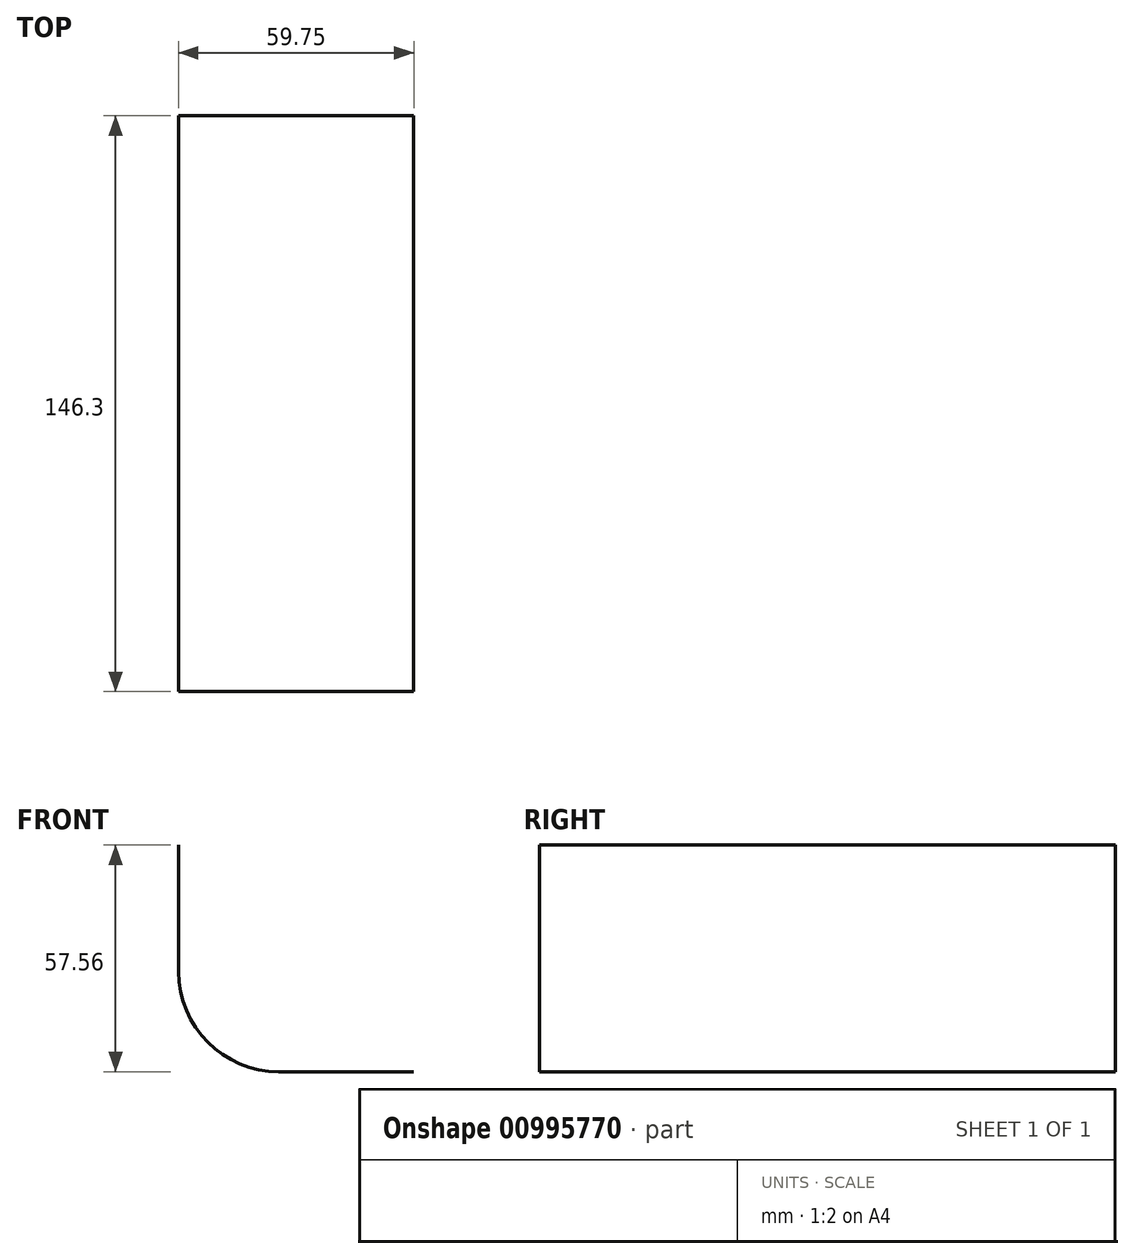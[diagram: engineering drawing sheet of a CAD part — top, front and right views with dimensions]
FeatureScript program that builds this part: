
annotation { "Feature Type Name" : "Feature", "Feature Type Description" : "" }
export const myFeature = defineFeature(function(context is Context, id is Id, definition is map)
    precondition{}
    {
        {
            var Q0;
            Q0=qCreatedBy(makeId("Front.planeOp"),FACE);
            var sketch = newSketch(context, id + "F0", { "sketchPlane" : qUnion([Q0])});
            skLineSegment(sketch, "E0", {"start": v(0, 57.56) * mm, "end": v(0, 0) * mm});
            skLineSegment(sketch, "E1", {"start": v(0, 0) * mm, "end": v(59.75, 0) * mm});
            skSolve(sketch);
        }
        {
            var Q0;
            Q0=sQuery(id+"F0.wireOp",EDGE,"1559505a-995c-4fc5-b292-b2fe923a3a53");
            var Q1;
            Q1=sQuery(id+"F0.wireOp",EDGE,"E1");
            var Q2;
            Q2=sQuery(id+"F0.wireOp",EDGE,"E0");
            extrude(context, id + "F1", {"bodyType" : ToolBodyType.SURFACE, "surfaceEntities" : qUnion([Q0, Q1, Q2]), "depth" : 146.3 * mm, "offsetDistance" : 25.4 * mm});
        }
        {
            var Q0;
            Q0=makeQuery(id+"F1.opExtrude","SWEPT_EDGE",EDGE,{"disambiguationData":[OSD([sQuery(id+"F0.wireOp",VERTEX,"E0.end")])]});
            fillet(context, id + "F2", {"entities" : qUnion([Q0]), "radius" : 25.4 * mm, "tangentPropagation" : true, "allowEdgeOverflow" : false});
        }
    });
